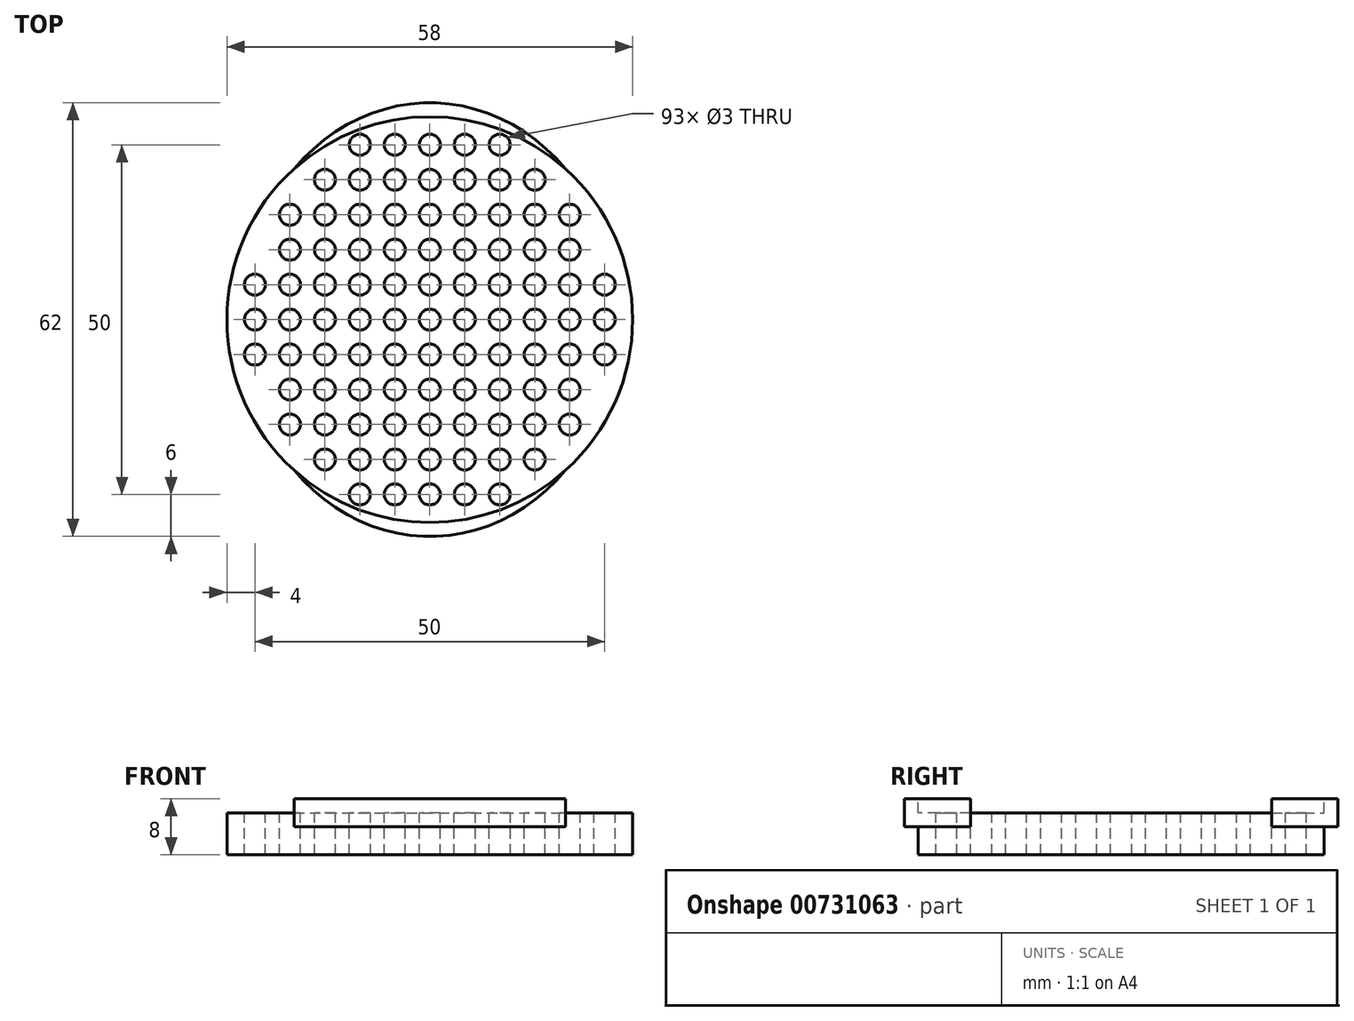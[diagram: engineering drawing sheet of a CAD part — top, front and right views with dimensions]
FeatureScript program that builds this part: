
annotation { "Feature Type Name" : "Feature", "Feature Type Description" : "" }
export const myFeature = defineFeature(function(context is Context, id is Id, definition is map)
    precondition{}
    {
        {
            var Q0;
            Q0=qCreatedBy(makeId("Top.planeOp"),FACE);
            var sketch = newSketch(context, id + "F0", { "sketchPlane" : qUnion([Q0])});
            skEllipse(sketch, "E0", {"center": v(0, 0) * mm, "majorRadius": 31 * mm, "minorRadius": 27 * mm, "majorAxis": v(0, 1)});
            skCircle(sketch, "E1", {"center": v(0, 0) * mm, "radius": 29 * mm});
            skCircle(sketch, "E2", {"center": v(0, 0) * mm, "radius": 1.5 * mm});
            skCircle(sketch, "E3.0.1.0", {"center": v(0, 5) * mm, "radius": 1.5 * mm});
            skCircle(sketch, "E3.0.2.0", {"center": v(0, 10) * mm, "radius": 1.5 * mm});
            skCircle(sketch, "E3.0.3.0", {"center": v(0, 15) * mm, "radius": 1.5 * mm});
            skCircle(sketch, "E3.0.4.0", {"center": v(0, 20) * mm, "radius": 1.5 * mm});
            skCircle(sketch, "E3.0.5.0", {"center": v(0, 25) * mm, "radius": 1.5 * mm});
            skCircle(sketch, "E3.1.0.0", {"center": v(5, 0) * mm, "radius": 1.5 * mm});
            skCircle(sketch, "E3.1.1.0", {"center": v(5, 5) * mm, "radius": 1.5 * mm});
            skCircle(sketch, "E3.1.2.0", {"center": v(5, 10) * mm, "radius": 1.5 * mm});
            skCircle(sketch, "E3.1.3.0", {"center": v(5, 15) * mm, "radius": 1.5 * mm});
            skCircle(sketch, "E3.1.4.0", {"center": v(5, 20) * mm, "radius": 1.5 * mm});
            skCircle(sketch, "E3.1.5.0", {"center": v(5, 25) * mm, "radius": 1.5 * mm});
            skCircle(sketch, "E3.2.0.0", {"center": v(10, 0) * mm, "radius": 1.5 * mm});
            skCircle(sketch, "E3.2.1.0", {"center": v(10, 5) * mm, "radius": 1.5 * mm});
            skCircle(sketch, "E3.2.2.0", {"center": v(10, 10) * mm, "radius": 1.5 * mm});
            skCircle(sketch, "E3.2.3.0", {"center": v(10, 15) * mm, "radius": 1.5 * mm});
            skCircle(sketch, "E3.2.4.0", {"center": v(10, 20) * mm, "radius": 1.5 * mm});
            skCircle(sketch, "E3.2.5.0", {"center": v(10, 25) * mm, "radius": 1.5 * mm});
            skCircle(sketch, "E3.3.0.0", {"center": v(15, 0) * mm, "radius": 1.5 * mm});
            skCircle(sketch, "E3.3.1.0", {"center": v(15, 5) * mm, "radius": 1.5 * mm});
            skCircle(sketch, "E3.3.2.0", {"center": v(15, 10) * mm, "radius": 1.5 * mm});
            skCircle(sketch, "E3.3.3.0", {"center": v(15, 15) * mm, "radius": 1.5 * mm});
            skCircle(sketch, "E3.3.4.0", {"center": v(15, 20) * mm, "radius": 1.5 * mm});
            skCircle(sketch, "E3.4.0.0", {"center": v(20, 0) * mm, "radius": 1.5 * mm});
            skCircle(sketch, "E3.4.1.0", {"center": v(20, 5) * mm, "radius": 1.5 * mm});
            skCircle(sketch, "E3.4.2.0", {"center": v(20, 10) * mm, "radius": 1.5 * mm});
            skCircle(sketch, "E3.4.3.0", {"center": v(20, 15) * mm, "radius": 1.5 * mm});
            skCircle(sketch, "E3.5.0.0", {"center": v(25, 0) * mm, "radius": 1.5 * mm});
            skCircle(sketch, "E3.5.1.0", {"center": v(25, 5) * mm, "radius": 1.5 * mm});
            skLineSegment(sketch, "E3.direction1", {"start": v(0, 0) * mm, "end": v(5, 0) * mm, "construction": true});
            skLineSegment(sketch, "E3.direction2", {"start": v(0, 0) * mm, "end": v(0, 5) * mm, "construction": true});
            skCircle(sketch, "E4.0.1.0", {"center": v(20, -10) * mm, "radius": 1.5 * mm});
            skCircle(sketch, "E4.0.1.1", {"center": v(5, -10) * mm, "radius": 1.5 * mm});
            skCircle(sketch, "E4.0.1.2", {"center": v(25, -5) * mm, "radius": 1.5 * mm});
            skCircle(sketch, "E4.0.1.3", {"center": v(15, -10) * mm, "radius": 1.5 * mm});
            skCircle(sketch, "E4.0.1.5", {"center": v(5, -25) * mm, "radius": 1.5 * mm});
            skCircle(sketch, "E4.0.1.6", {"center": v(0, -25) * mm, "radius": 1.5 * mm});
            skCircle(sketch, "E4.0.1.7", {"center": v(0, -20) * mm, "radius": 1.5 * mm});
            skCircle(sketch, "E4.0.1.8", {"center": v(0, -5) * mm, "radius": 1.5 * mm});
            skCircle(sketch, "E4.0.1.9", {"center": v(10, -15) * mm, "radius": 1.5 * mm});
            skCircle(sketch, "E4.0.1.12", {"center": v(0, -15) * mm, "radius": 1.5 * mm});
            skCircle(sketch, "E4.0.1.13", {"center": v(5, -20) * mm, "radius": 1.5 * mm});
            skCircle(sketch, "E4.0.1.14", {"center": v(5, -15) * mm, "radius": 1.5 * mm});
            skCircle(sketch, "E4.0.1.15", {"center": v(5, -5) * mm, "radius": 1.5 * mm});
            skCircle(sketch, "E4.0.1.17", {"center": v(15, -20) * mm, "radius": 1.5 * mm});
            skLineSegment(sketch, "E4.0.1.18", {"start": v(0, -30) * mm, "end": v(0, -25) * mm, "construction": true});
            skCircle(sketch, "E4.0.1.19", {"center": v(15, -5) * mm, "radius": 1.5 * mm});
            skCircle(sketch, "E4.0.1.20", {"center": v(15, -15) * mm, "radius": 1.5 * mm});
            skCircle(sketch, "E4.0.1.21", {"center": v(20, -5) * mm, "radius": 1.5 * mm});
            skCircle(sketch, "E4.0.1.24", {"center": v(10, -10) * mm, "radius": 1.5 * mm});
            skCircle(sketch, "E4.0.1.26", {"center": v(20, -15) * mm, "radius": 1.5 * mm});
            skCircle(sketch, "E4.0.1.29", {"center": v(10, -20) * mm, "radius": 1.5 * mm});
            skCircle(sketch, "E4.0.1.34", {"center": v(10, -5) * mm, "radius": 1.5 * mm});
            skCircle(sketch, "E4.0.1.35", {"center": v(0, -10) * mm, "radius": 1.5 * mm});
            skCircle(sketch, "E4.0.1.37", {"center": v(10, -25) * mm, "radius": 1.5 * mm});
            skCircle(sketch, "E4.1.0.0", {"center": v(-10, 20) * mm, "radius": 1.5 * mm});
            skCircle(sketch, "E4.1.0.2", {"center": v(-5, 25) * mm, "radius": 1.5 * mm});
            skCircle(sketch, "E4.1.0.3", {"center": v(-15, 20) * mm, "radius": 1.5 * mm});
            skCircle(sketch, "E4.1.0.4", {"center": v(-15, 5) * mm, "radius": 1.5 * mm});
            skCircle(sketch, "E4.1.0.5", {"center": v(-25, 5) * mm, "radius": 1.5 * mm});
            skCircle(sketch, "E4.1.0.9", {"center": v(-20, 15) * mm, "radius": 1.5 * mm});
            skCircle(sketch, "E4.1.0.10", {"center": v(-10, 5) * mm, "radius": 1.5 * mm});
            skCircle(sketch, "E4.1.0.11", {"center": v(-5, 5) * mm, "radius": 1.5 * mm});
            skCircle(sketch, "E4.1.0.16", {"center": v(-5, 15) * mm, "radius": 1.5 * mm});
            skCircle(sketch, "E4.1.0.17", {"center": v(-15, 10) * mm, "radius": 1.5 * mm});
            skCircle(sketch, "E4.1.0.20", {"center": v(-15, 15) * mm, "radius": 1.5 * mm});
            skCircle(sketch, "E4.1.0.21", {"center": v(-10, 25) * mm, "radius": 1.5 * mm});
            skLineSegment(sketch, "E4.1.0.22", {"start": v(-30, 0) * mm, "end": v(-25, 0) * mm, "construction": true});
            skCircle(sketch, "E4.1.0.23", {"center": v(-10, 0) * mm, "radius": 1.5 * mm});
            skCircle(sketch, "E4.1.0.25", {"center": v(-15, 0) * mm, "radius": 1.5 * mm});
            skCircle(sketch, "E4.1.0.26", {"center": v(-10, 15) * mm, "radius": 1.5 * mm});
            skCircle(sketch, "E4.1.0.27", {"center": v(-5, 20) * mm, "radius": 1.5 * mm});
            skCircle(sketch, "E4.1.0.28", {"center": v(-5, 10) * mm, "radius": 1.5 * mm});
            skCircle(sketch, "E4.1.0.29", {"center": v(-20, 10) * mm, "radius": 1.5 * mm});
            skCircle(sketch, "E4.1.0.30", {"center": v(-5, 0) * mm, "radius": 1.5 * mm});
            skCircle(sketch, "E4.1.0.31", {"center": v(-10, 10) * mm, "radius": 1.5 * mm});
            skCircle(sketch, "E4.1.0.32", {"center": v(-25, 0) * mm, "radius": 1.5 * mm});
            skCircle(sketch, "E4.1.0.33", {"center": v(-20, 0) * mm, "radius": 1.5 * mm});
            skCircle(sketch, "E4.1.0.37", {"center": v(-20, 5) * mm, "radius": 1.5 * mm});
            skCircle(sketch, "E4.1.1.0", {"center": v(-10, -10) * mm, "radius": 1.5 * mm});
            skCircle(sketch, "E4.1.1.2", {"center": v(-5, -5) * mm, "radius": 1.5 * mm});
            skCircle(sketch, "E4.1.1.3", {"center": v(-15, -10) * mm, "radius": 1.5 * mm});
            skCircle(sketch, "E4.1.1.9", {"center": v(-20, -15) * mm, "radius": 1.5 * mm});
            skCircle(sketch, "E4.1.1.10", {"center": v(-10, -25) * mm, "radius": 1.5 * mm});
            skCircle(sketch, "E4.1.1.11", {"center": v(-5, -25) * mm, "radius": 1.5 * mm});
            skCircle(sketch, "E4.1.1.15", {"center": v(-25, -5) * mm, "radius": 1.5 * mm});
            skCircle(sketch, "E4.1.1.16", {"center": v(-5, -15) * mm, "radius": 1.5 * mm});
            skCircle(sketch, "E4.1.1.17", {"center": v(-15, -20) * mm, "radius": 1.5 * mm});
            skCircle(sketch, "E4.1.1.19", {"center": v(-15, -5) * mm, "radius": 1.5 * mm});
            skCircle(sketch, "E4.1.1.20", {"center": v(-15, -15) * mm, "radius": 1.5 * mm});
            skCircle(sketch, "E4.1.1.21", {"center": v(-10, -5) * mm, "radius": 1.5 * mm});
            skCircle(sketch, "E4.1.1.24", {"center": v(-20, -10) * mm, "radius": 1.5 * mm});
            skCircle(sketch, "E4.1.1.26", {"center": v(-10, -15) * mm, "radius": 1.5 * mm});
            skCircle(sketch, "E4.1.1.27", {"center": v(-5, -10) * mm, "radius": 1.5 * mm});
            skCircle(sketch, "E4.1.1.28", {"center": v(-5, -20) * mm, "radius": 1.5 * mm});
            skCircle(sketch, "E4.1.1.31", {"center": v(-10, -20) * mm, "radius": 1.5 * mm});
            skCircle(sketch, "E4.1.1.34", {"center": v(-20, -5) * mm, "radius": 1.5 * mm});
            skLineSegment(sketch, "E4.direction1", {"start": v(0, 0) * mm, "end": v(-30, 0) * mm, "construction": true});
            skLineSegment(sketch, "E4.direction2", {"start": v(0, 0) * mm, "end": v(0, -30) * mm, "construction": true});
            skSolve(sketch);
        }
        {
            var Q0;
            {var subQ0=sQuery(id+"F0.wireOp",EDGE,"E1");var subQ1=sQuery(id+"F0.wireOp",EDGE,"E0");var subQ2=makeQuery(id+"F0.imprint","INTERSECT",VERTEX,{"disambiguationData":[OD(0.0)],"derivedFrom":[subQ1,subQ0]});Q0=makeQuery(id+"F0.imprint","IMPRINT",FACE,{"disambiguationData":[TD([[makeQuery(id+"F0.imprint","IMPRINT",EDGE,{"disambiguationData":[TD([[subQ2,1.0]])],"derivedFrom":subQ1}),1.0]])]});}
            var Q1;
            {var subQ0=sQuery(id+"F0.wireOp",EDGE,"E1");var subQ1=sQuery(id+"F0.wireOp",EDGE,"E0");var subQ2=makeQuery(id+"F0.imprint","INTERSECT",VERTEX,{"disambiguationData":[OD(0.0)],"derivedFrom":[subQ1,subQ0]});Q1=makeQuery(id+"F0.imprint","IMPRINT",FACE,{"disambiguationData":[TD([[makeQuery(id+"F0.imprint","IMPRINT",EDGE,{"disambiguationData":[TD([[subQ2,1.0]])],"derivedFrom":subQ1}),-1.0]])]});}
            var Q2;
            {var subQ0=sQuery(id+"F0.wireOp",EDGE,"E1");var subQ1=sQuery(id+"F0.wireOp",EDGE,"E0");var subQ2=makeQuery(id+"F0.imprint","INTERSECT",VERTEX,{"disambiguationData":[OD(2.0)],"derivedFrom":[subQ1,subQ0]});Q2=makeQuery(id+"F0.imprint","IMPRINT",FACE,{"disambiguationData":[TD([[makeQuery(id+"F0.imprint","IMPRINT",EDGE,{"disambiguationData":[TD([[subQ2,-1.0]])],"derivedFrom":subQ1}),-1.0]])]});}
            extrude(context, id + "F1", {"entities" : qUnion([Q0, Q1, Q2]), "oppositeDirection" : true, "depth" : 10 * mm, "offsetDistance" : 25 * mm});
        }
        {
            var Q0;
            {var subQ0=sQuery(id+"F0.wireOp",EDGE,"E1");var subQ1=sQuery(id+"F0.wireOp",EDGE,"E0");var subQ2=makeQuery(id+"F0.imprint","INTERSECT",VERTEX,{"disambiguationData":[OD(0.0)],"derivedFrom":[subQ1,subQ0]});Q0=makeQuery(id+"F0.imprint","IMPRINT",FACE,{"disambiguationData":[TD([[makeQuery(id+"F0.imprint","IMPRINT",EDGE,{"disambiguationData":[TD([[subQ2,1.0]])],"derivedFrom":subQ1}),-1.0]])]});}
            var Q1;
            {var subQ0=sQuery(id+"F0.wireOp",EDGE,"E1");var subQ1=sQuery(id+"F0.wireOp",EDGE,"E0");var subQ2=makeQuery(id+"F0.imprint","INTERSECT",VERTEX,{"disambiguationData":[OD(0.0)],"derivedFrom":[subQ1,subQ0]});Q1=makeQuery(id+"F0.imprint","IMPRINT",FACE,{"disambiguationData":[TD([[makeQuery(id+"F0.imprint","IMPRINT",EDGE,{"disambiguationData":[TD([[subQ2,1.0]])],"derivedFrom":subQ1}),1.0]])]});}
            var Q2;
            {var subQ0=sQuery(id+"F0.wireOp",EDGE,"E1");var subQ1=sQuery(id+"F0.wireOp",EDGE,"E0");var subQ2=makeQuery(id+"F0.imprint","INTERSECT",VERTEX,{"disambiguationData":[OD(2.0)],"derivedFrom":[subQ1,subQ0]});Q2=makeQuery(id+"F0.imprint","IMPRINT",FACE,{"disambiguationData":[TD([[makeQuery(id+"F0.imprint","IMPRINT",EDGE,{"disambiguationData":[TD([[subQ2,-1.0]])],"derivedFrom":subQ1}),-1.0]])]});}
            extrude(context, id + "F2", {"entities" : qUnion([Q0, Q1, Q2]), "operationType" : NewBodyOperationType.REMOVE, "oppositeDirection" : true, "depth" : 4 * mm, "offsetDistance" : 25 * mm});
        }
        {
            var Q0;
            {var subQ0=sQuery(id+"F0.wireOp",EDGE,"E1");var subQ1=sQuery(id+"F0.wireOp",EDGE,"E0");var subQ2=makeQuery(id+"F0.imprint","INTERSECT",VERTEX,{"disambiguationData":[OD(1.0)],"derivedFrom":[subQ1,subQ0]});Q0=makeQuery(id+"F0.imprint","IMPRINT",FACE,{"disambiguationData":[TD([[makeQuery(id+"F0.imprint","IMPRINT",EDGE,{"disambiguationData":[TD([[subQ2,1.0]])],"derivedFrom":subQ1}),1.0]])]});}
            var Q1;
            {var subQ0=sQuery(id+"F0.wireOp",EDGE,"E1");var subQ1=sQuery(id+"F0.wireOp",EDGE,"E0");var subQ2=makeQuery(id+"F0.imprint","INTERSECT",VERTEX,{"disambiguationData":[OD(0.0)],"derivedFrom":[subQ1,subQ0]});Q1=makeQuery(id+"F0.imprint","IMPRINT",FACE,{"disambiguationData":[TD([[makeQuery(id+"F0.imprint","IMPRINT",EDGE,{"disambiguationData":[TD([[subQ2,-1.0]])],"derivedFrom":subQ1}),1.0]])]});}
            extrude(context, id + "F3", {"entities" : qUnion([Q0, Q1]), "operationType" : NewBodyOperationType.ADD, "oppositeDirection" : true, "depth" : 6 * mm, "offsetDistance" : 25 * mm});
        }
        {
            var Q0;
            {var subQ0=sQuery(id+"F0.wireOp",EDGE,"E1");var subQ1=sQuery(id+"F0.wireOp",EDGE,"E0");var subQ2=makeQuery(id+"F0.imprint","INTERSECT",VERTEX,{"disambiguationData":[OD(1.0)],"derivedFrom":[subQ1,subQ0]});Q0=makeQuery(id+"F0.imprint","IMPRINT",FACE,{"disambiguationData":[TD([[makeQuery(id+"F0.imprint","IMPRINT",EDGE,{"disambiguationData":[TD([[subQ2,1.0]])],"derivedFrom":subQ1}),1.0]])]});}
            var Q1;
            {var subQ0=sQuery(id+"F0.wireOp",EDGE,"E1");var subQ1=sQuery(id+"F0.wireOp",EDGE,"E0");var subQ2=makeQuery(id+"F0.imprint","INTERSECT",VERTEX,{"disambiguationData":[OD(0.0)],"derivedFrom":[subQ1,subQ0]});Q1=makeQuery(id+"F0.imprint","IMPRINT",FACE,{"disambiguationData":[TD([[makeQuery(id+"F0.imprint","IMPRINT",EDGE,{"disambiguationData":[TD([[subQ2,-1.0]])],"derivedFrom":subQ1}),1.0]])]});}
            extrude(context, id + "F4", {"entities" : qUnion([Q0, Q1]), "operationType" : NewBodyOperationType.REMOVE, "oppositeDirection" : true, "depth" : 2 * mm, "offsetDistance" : 25 * mm});
        }
    });
